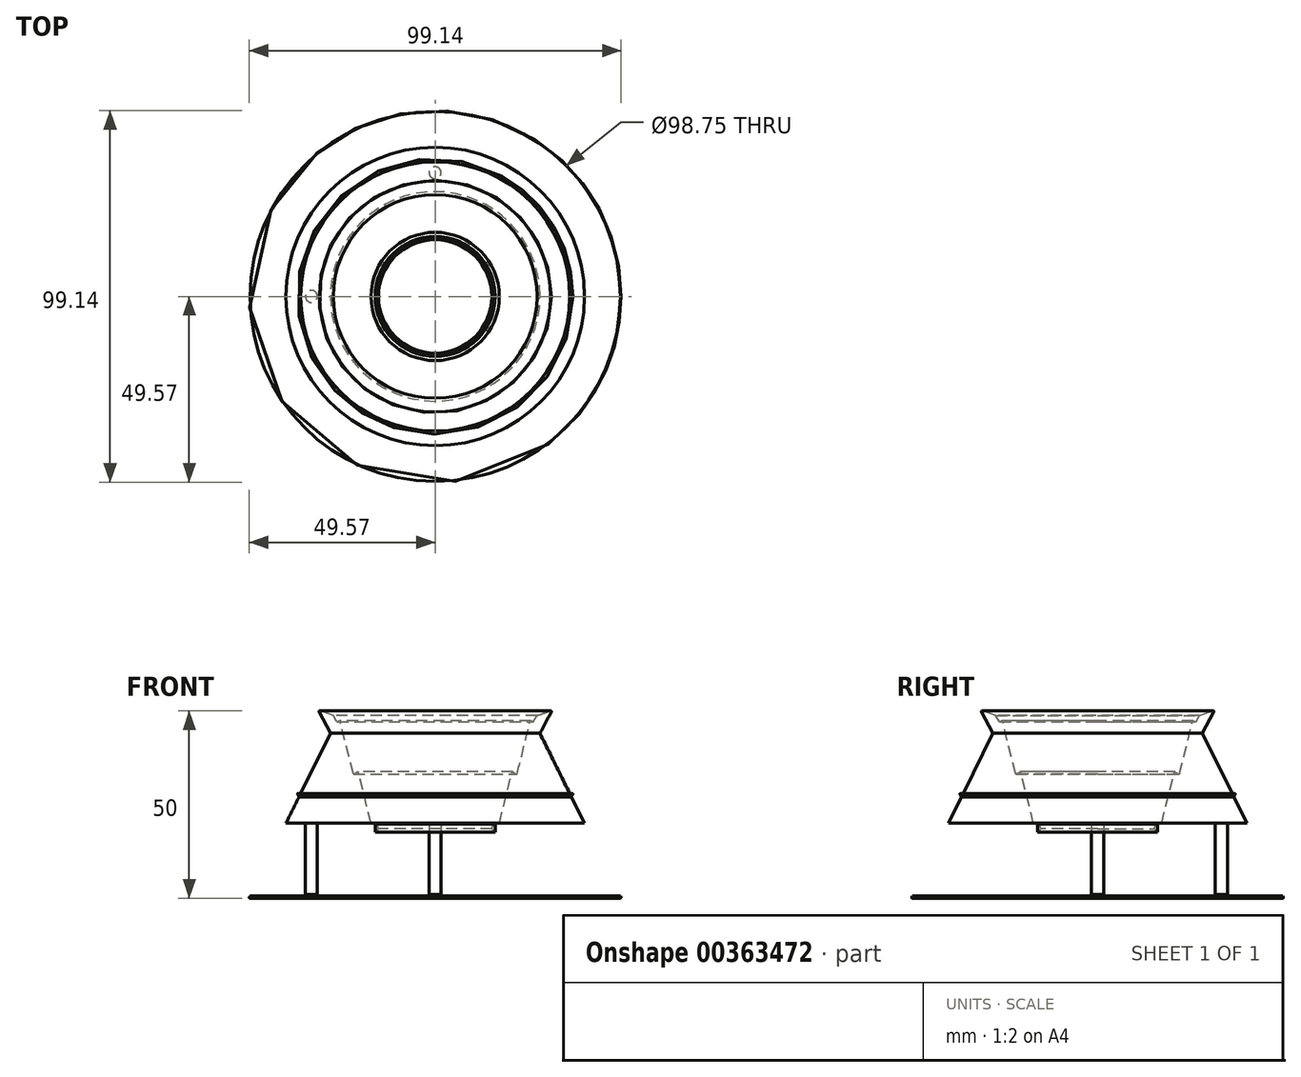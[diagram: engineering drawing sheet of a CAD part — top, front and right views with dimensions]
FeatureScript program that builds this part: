
annotation { "Feature Type Name" : "Feature", "Feature Type Description" : "" }
export const myFeature = defineFeature(function(context is Context, id is Id, definition is map)
    precondition{}
    {
        {
            var Q0;
            Q0=qCreatedBy(makeId("Front.planeOp"),FACE);
            var sketch = newSketch(context, id + "F0", { "sketchPlane" : qUnion([Q0])});
            skLineSegment(sketch, "E0", {"start": v(-27.94, 44) * mm, "end": v(-49.55, 0.29) * mm, "construction": true});
            skLineSegment(sketch, "E1", {"start": v(-30.99, 49.7) * mm, "end": v(-27.94, 44) * mm});
            skLineSegment(sketch, "E2", {"start": v(-42.47, 14.63) * mm, "end": v(-42.86, 15.36) * mm});
            skLineSegment(sketch, "E3", {"start": v(-36.32, 27.05) * mm, "end": v(-36.71, 27.79) * mm});
            skLineSegment(sketch, "E4", {"start": v(-42.77, 15.5) * mm, "end": v(-42.03, 15.5) * mm});
            skLineSegment(sketch, "E5", {"start": v(-36.62, 27.94) * mm, "end": v(-35.88, 27.94) * mm});
            skLineSegment(sketch, "E6", {"start": v(-49.7, 0) * mm, "end": v(-42.47, 14.63) * mm});
            skLineSegment(sketch, "E7", {"start": v(-42.03, 15.5) * mm, "end": v(-36.32, 27.05) * mm});
            skLineSegment(sketch, "E8", {"start": v(-35.88, 27.94) * mm, "end": v(-27.94, 44) * mm});
            skLineSegment(sketch, "E9", {"start": v(0, 73.17) * mm, "end": v(0, -71.04) * mm, "construction": true});
            skLineSegment(sketch, "E10", {"start": v(-16.8, 19.3) * mm, "end": v(-15.83, 19.84) * mm});
            skLineSegment(sketch, "E11", {"start": v(-21.72, 33.14) * mm, "end": v(-20.75, 33.68) * mm});
            skLineSegment(sketch, "E12", {"start": v(-20.46, 33.55) * mm, "end": v(-16.95, 19.37) * mm});
            skLineSegment(sketch, "E13", {"start": v(-25.37, 47.32) * mm, "end": v(-21.87, 33.2) * mm});
            skLineSegment(sketch, "E14", {"start": v(-26.22, 47.14) * mm, "end": v(-27.17, 48.72) * mm});
            skPoint(sketch, "E15.visualSharp", {"position": v(-31.14, 50) * mm});
            skArc(sketch, "E15.filletArc", {"start": v(-30.81, 50) * mm, "mid": v(-30.98, 49.9) * mm, "end": v(-30.99, 49.7) * mm});
            skPoint(sketch, "E16.visualSharp", {"position": v(-20.53, 33.8) * mm});
            skArc(sketch, "E16.filletArc", {"start": v(-20.46, 33.55) * mm, "mid": v(-20.58, 33.69) * mm, "end": v(-20.75, 33.68) * mm});
            skPoint(sketch, "E17.visualSharp", {"position": v(-15.6, 19.97) * mm});
            skArc(sketch, "E17.filletArc", {"start": v(-15.54, 19.72) * mm, "mid": v(-15.66, 19.85) * mm, "end": v(-15.83, 19.84) * mm});
            skPoint(sketch, "E18.visualSharp", {"position": v(-49.7, 0) * mm});
            skArc(sketch, "E18.filletArc", {"start": v(-49.55, 0.29) * mm, "mid": v(-49.54, 0.1) * mm, "end": v(-49.37, 0) * mm});
            skPoint(sketch, "E19.visualSharp", {"position": v(-36.8, 27.94) * mm});
            skArc(sketch, "E19.filletArc", {"start": v(-36.62, 27.94) * mm, "mid": v(-36.71, 27.89) * mm, "end": v(-36.71, 27.79) * mm});
            skPoint(sketch, "E20.visualSharp", {"position": v(-42.94, 15.5) * mm});
            skArc(sketch, "E20.filletArc", {"start": v(-42.77, 15.5) * mm, "mid": v(-42.86, 15.46) * mm, "end": v(-42.86, 15.36) * mm});
            skLineSegment(sketch, "E21", {"start": v(-26.1, 47.1) * mm, "end": v(-25.5, 47.4) * mm});
            skPoint(sketch, "E22.visualSharp", {"position": v(-21.84, 33.08) * mm});
            skArc(sketch, "E22.filletArc", {"start": v(-21.87, 33.2) * mm, "mid": v(-21.81, 33.14) * mm, "end": v(-21.72, 33.14) * mm});
            skPoint(sketch, "E23.visualSharp", {"position": v(-16.92, 19.24) * mm});
            skArc(sketch, "E23.filletArc", {"start": v(-16.95, 19.37) * mm, "mid": v(-16.9, 19.3) * mm, "end": v(-16.8, 19.3) * mm});
            skPoint(sketch, "E24.visualSharp", {"position": v(-26.17, 47.07) * mm});
            skArc(sketch, "E24.filletArc", {"start": v(-26.22, 47.14) * mm, "mid": v(-26.16, 47.1) * mm, "end": v(-26.1, 47.1) * mm});
            skPoint(sketch, "E25.visualSharp", {"position": v(-25.4, 47.44) * mm});
            skArc(sketch, "E25.filletArc", {"start": v(-25.37, 47.32) * mm, "mid": v(-25.42, 47.4) * mm, "end": v(-25.5, 47.4) * mm});
            skLineSegment(sketch, "E26", {"start": v(-16, 0) * mm, "end": v(-49.37, 0) * mm});
            skLineSegment(sketch, "E27", {"start": v(-16, 0) * mm, "end": v(-16, 9.72) * mm});
            skLineSegment(sketch, "E28", {"start": v(-16, 9.72) * mm, "end": v(-16, 17.65) * mm});
            skLineSegment(sketch, "E29", {"start": v(-16, 17.65) * mm, "end": v(-15.12, 18.53) * mm});
            skLineSegment(sketch, "E30", {"start": v(-15.12, 18.53) * mm, "end": v(-15.54, 19.72) * mm});
            skLineSegment(sketch, "E31", {"start": v(-30.81, 50) * mm, "end": v(-27.17, 48.72) * mm});
            skSolve(sketch);
        }
        {
            var Q0;
            Q0=makeQuery(id+"F0.imprint","IMPRINT",FACE,{"disambiguationData":[TD([[makeQuery(id+"F0.imprint","IMPRINT",EDGE,{"derivedFrom":sQuery(id+"F0.wireOp",EDGE,"E1")}),1.0]])]});
            var Q1;
            Q1=sQuery(id+"F0.wireOp",EDGE,"E9");
            revolve(context, id + "F1", {"entities" : qUnion([Q0]), "axis" : qUnion([Q1]), "revolveType" : RevolveType.FULL});
        }
        {
            var Q0;
            Q0=makeQuery(id+"F1.opRevolve","SWEPT_FACE",FACE,{"disambiguationData":[OSD([sQuery(id+"F0.wireOp",EDGE,"E26")])]});
            var sketch = newSketch(context, id + "F2", { "sketchPlane" : qUnion([Q0])});
            skCircle(sketch, "E32", {"center": v(33, 0) * mm, "radius": 1.6 * mm});
            skCircle(sketch, "E33", {"center": v(0, 33) * mm, "radius": 1.6 * mm});
            skCircle(sketch, "E34.MirrorC", {"center": v(0, -33) * mm, "radius": 1.6 * mm});
            skCircle(sketch, "E35.MirrorC", {"center": v(-33, 0) * mm, "radius": 1.6 * mm});
            skSolve(sketch);
        }
        {
            var Q0;
            Q0=makeQuery(id+"F2.imprint","IMPRINT",FACE,{"disambiguationData":[TD([[makeQuery(id+"F2.imprint","IMPRINT",EDGE,{"derivedFrom":sQuery(id+"F2.wireOp",EDGE,"E32")}),1.0]])]});
            var Q1;
            Q1=makeQuery(id+"F2.imprint","IMPRINT",FACE,{"disambiguationData":[TD([[makeQuery(id+"F2.imprint","IMPRINT",EDGE,{"derivedFrom":sQuery(id+"F2.wireOp",EDGE,"E34.MirrorC")}),-1.0]])]});
            var Q2;
            Q2=makeQuery(id+"F2.imprint","IMPRINT",FACE,{"disambiguationData":[TD([[makeQuery(id+"F2.imprint","IMPRINT",EDGE,{"derivedFrom":sQuery(id+"F2.wireOp",EDGE,"E33")}),1.0]])]});
            var Q3;
            Q3=makeQuery(id+"F2.imprint","IMPRINT",FACE,{"disambiguationData":[TD([[makeQuery(id+"F2.imprint","IMPRINT",EDGE,{"derivedFrom":sQuery(id+"F2.wireOp",EDGE,"E35.MirrorC")}),-1.0]])]});
            extrude(context, id + "F3", {"entities" : qUnion([Q0, Q1, Q2, Q3]), "operationType" : NewBodyOperationType.REMOVE, "oppositeDirection" : true, "depth" : 20 * mm});
        }
        {
            var Q0;
            Q0 = qSketchRegion(id + "F2", true);
            extrude(context, id + "F4", {"entities" : qUnion([Q0]), "operationType" : NewBodyOperationType.REMOVE, "oppositeDirection" : true, "depth" : 1 * mm});
        }
    });
